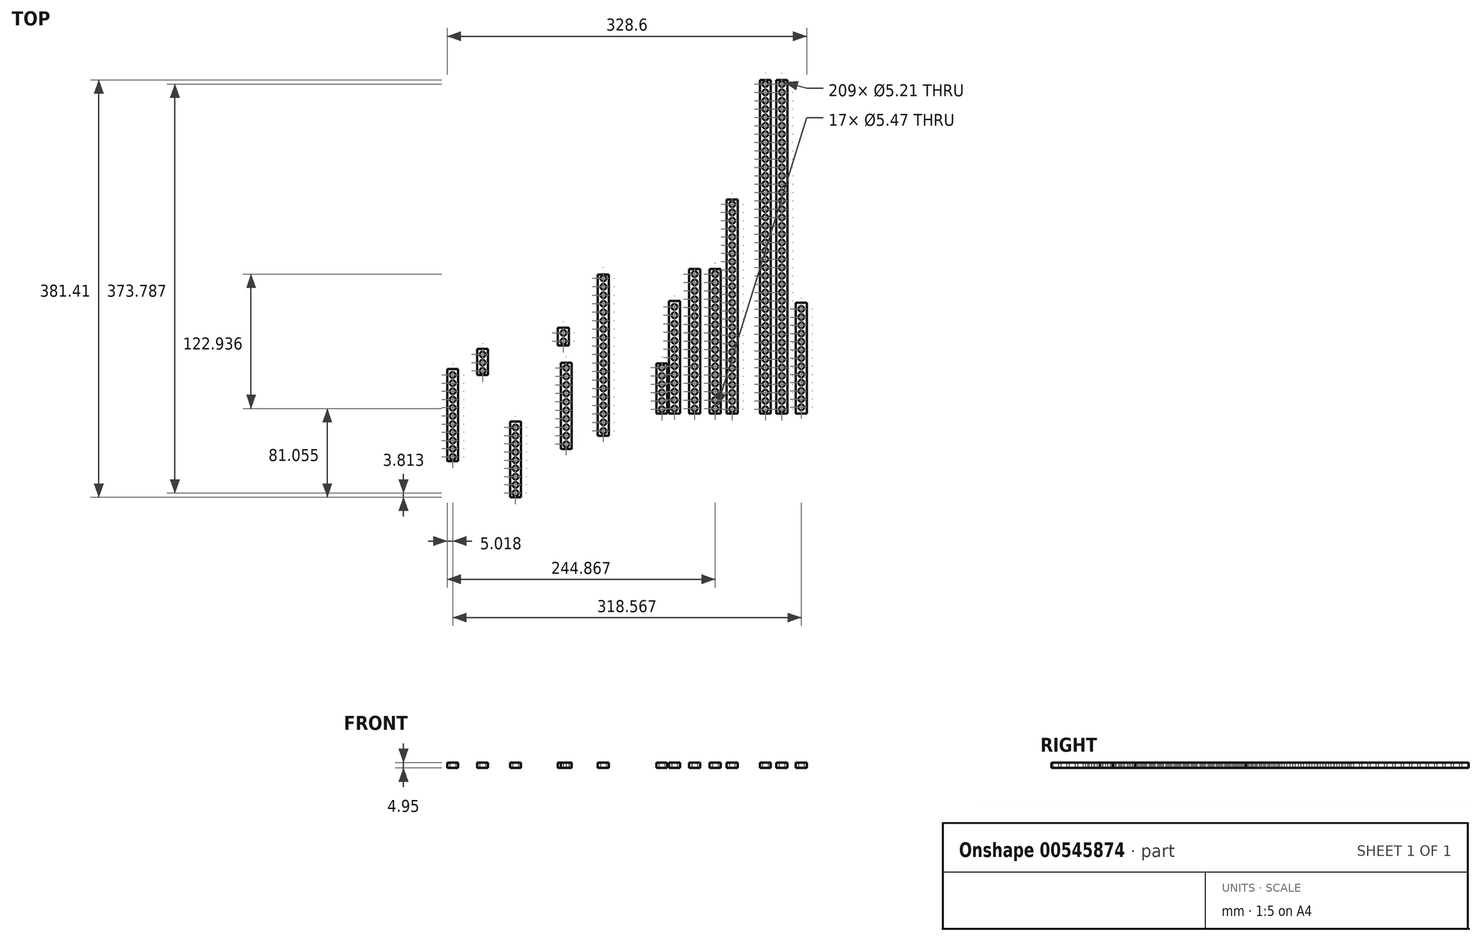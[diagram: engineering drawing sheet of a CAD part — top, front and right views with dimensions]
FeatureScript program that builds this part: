
annotation { "Feature Type Name" : "Feature", "Feature Type Description" : "" }
export const myFeature = defineFeature(function(context is Context, id is Id, definition is map)
    precondition{}
    {
        {
            var Q0;
            Q0=qCreatedBy(makeId("Top.planeOp"),FACE);
            var sketch = newSketch(context, id + "F0", { "sketchPlane" : qUnion([Q0])});
            skLineSegment(sketch, "E0.bottom", {"start": v(-63.67, 0) * mm, "end": v(-53.64, 0) * mm});
            skLineSegment(sketch, "E0.top", {"start": v(-63.67, 102.87) * mm, "end": v(-53.64, 102.87) * mm});
            skLineSegment(sketch, "E0.left", {"start": v(-63.67, 0) * mm, "end": v(-63.67, 102.87) * mm});
            skLineSegment(sketch, "E0.right", {"start": v(-53.64, 0) * mm, "end": v(-53.64, 102.87) * mm});
            skCircle(sketch, "E1", {"center": v(-58.66, 4.45) * mm, "radius": 2.6 * mm});
            skPoint(sketch, "E1.centerSnap0", {"position": v(-58.66, 0) * mm});
            skCircle(sketch, "E2.0.1.0", {"center": v(-58.66, 12.2) * mm, "radius": 2.6 * mm});
            skCircle(sketch, "E2.0.2.0", {"center": v(-58.66, 19.94) * mm, "radius": 2.6 * mm});
            skCircle(sketch, "E2.0.3.0", {"center": v(-58.66, 27.69) * mm, "radius": 2.6 * mm});
            skCircle(sketch, "E2.0.4.0", {"center": v(-58.66, 35.43) * mm, "radius": 2.6 * mm});
            skCircle(sketch, "E2.0.5.0", {"center": v(-58.66, 43.18) * mm, "radius": 2.6 * mm});
            skCircle(sketch, "E2.0.6.0", {"center": v(-58.66, 50.93) * mm, "radius": 2.6 * mm});
            skCircle(sketch, "E2.0.7.0", {"center": v(-58.66, 58.67) * mm, "radius": 2.6 * mm});
            skCircle(sketch, "E2.0.8.0", {"center": v(-58.66, 66.42) * mm, "radius": 2.6 * mm});
            skCircle(sketch, "E2.0.9.0", {"center": v(-58.66, 74.17) * mm, "radius": 2.6 * mm});
            skCircle(sketch, "E2.0.10.0", {"center": v(-58.66, 81.92) * mm, "radius": 2.6 * mm});
            skCircle(sketch, "E2.0.11.0", {"center": v(-58.66, 89.66) * mm, "radius": 2.6 * mm});
            skCircle(sketch, "E2.0.12.0", {"center": v(-58.66, 97.4) * mm, "radius": 2.6 * mm});
            skLineSegment(sketch, "E2.direction1", {"start": v(-58.66, 4.45) * mm, "end": v(-33.26, 4.45) * mm, "construction": true});
            skLineSegment(sketch, "E2.direction2", {"start": v(-58.66, 4.45) * mm, "end": v(-58.66, 12.2) * mm, "construction": true});
            skSolve(sketch);
        }
        {
            var Q0;
            Q0=makeQuery(id+"F0.imprint","IMPRINT",FACE,{"disambiguationData":[TD([[makeQuery(id+"F0.imprint","IMPRINT",EDGE,{"derivedFrom":sQuery(id+"F0.wireOp",EDGE,"E0.bottom")}),1.0]])]});
            extrude(context, id + "F1", {"entities" : qUnion([Q0]), "depth" : 4.95 * mm, "offsetDistance" : 25.4 * mm});
        }
        {
            var Q0;
            Q0=qCreatedBy(makeId("Top.planeOp"),FACE);
            var sketch = newSketch(context, id + "F2", { "sketchPlane" : qUnion([Q0])});
            skLineSegment(sketch, "E3.bottom", {"start": v(-45.23, 0) * mm, "end": v(-35.2, 0) * mm});
            skLineSegment(sketch, "E3.top", {"start": v(-45.23, 132.08) * mm, "end": v(-35.2, 132.08) * mm});
            skLineSegment(sketch, "E3.left", {"start": v(-45.23, 0) * mm, "end": v(-45.23, 132.08) * mm});
            skLineSegment(sketch, "E3.right", {"start": v(-35.2, 0) * mm, "end": v(-35.2, 132.08) * mm});
            skCircle(sketch, "E4", {"center": v(-40.2, 4.44) * mm, "radius": 2.6 * mm});
            skPoint(sketch, "E4.centerSnap0", {"position": v(-40.2, 0) * mm});
            skCircle(sketch, "E5.0.1.0", {"center": v(-40.2, 12.13) * mm, "radius": 2.6 * mm});
            skCircle(sketch, "E5.0.2.0", {"center": v(-40.2, 19.81) * mm, "radius": 2.6 * mm});
            skCircle(sketch, "E5.0.3.0", {"center": v(-40.2, 27.5) * mm, "radius": 2.6 * mm});
            skCircle(sketch, "E5.0.4.0", {"center": v(-40.2, 35.18) * mm, "radius": 2.6 * mm});
            skCircle(sketch, "E5.0.5.0", {"center": v(-40.2, 42.86) * mm, "radius": 2.6 * mm});
            skCircle(sketch, "E5.0.6.0", {"center": v(-40.2, 50.55) * mm, "radius": 2.6 * mm});
            skCircle(sketch, "E5.0.7.0", {"center": v(-40.2, 58.23) * mm, "radius": 2.6 * mm});
            skCircle(sketch, "E5.0.8.0", {"center": v(-40.2, 65.91) * mm, "radius": 2.6 * mm});
            skCircle(sketch, "E5.0.9.0", {"center": v(-40.2, 73.6) * mm, "radius": 2.6 * mm});
            skCircle(sketch, "E5.0.10.0", {"center": v(-40.2, 81.28) * mm, "radius": 2.6 * mm});
            skCircle(sketch, "E5.0.11.0", {"center": v(-40.2, 88.96) * mm, "radius": 2.6 * mm});
            skCircle(sketch, "E5.0.12.0", {"center": v(-40.2, 96.65) * mm, "radius": 2.6 * mm});
            skCircle(sketch, "E5.0.13.0", {"center": v(-40.2, 104.33) * mm, "radius": 2.6 * mm});
            skCircle(sketch, "E5.0.14.0", {"center": v(-40.2, 112.01) * mm, "radius": 2.6 * mm});
            skCircle(sketch, "E5.0.15.0", {"center": v(-40.2, 119.7) * mm, "radius": 2.6 * mm});
            skCircle(sketch, "E5.0.16.0", {"center": v(-40.2, 127.38) * mm, "radius": 2.6 * mm});
            skLineSegment(sketch, "E5.direction1", {"start": v(-40.2, 4.44) * mm, "end": v(-14.8, 4.45) * mm, "construction": true});
            skLineSegment(sketch, "E5.direction2", {"start": v(-40.2, 4.44) * mm, "end": v(-40.2, 12.13) * mm, "construction": true});
            skSolve(sketch);
        }
        {
            var Q0;
            Q0=makeQuery(id+"F2.imprint","IMPRINT",FACE,{"disambiguationData":[TD([[makeQuery(id+"F2.imprint","IMPRINT",EDGE,{"derivedFrom":sQuery(id+"F2.wireOp",EDGE,"E3.bottom")}),1.0]])]});
            extrude(context, id + "F3", {"entities" : qUnion([Q0]), "depth" : 4.95 * mm, "offsetDistance" : 25.4 * mm});
        }
        {
            var Q0;
            Q0=qCreatedBy(makeId("Top.planeOp"),FACE);
            var sketch = newSketch(context, id + "F4", { "sketchPlane" : qUnion([Q0])});
            skLineSegment(sketch, "E6.bottom", {"start": v(-26.44, 0) * mm, "end": v(-16.4, 0) * mm});
            skLineSegment(sketch, "E6.top", {"start": v(-26.44, 132.08) * mm, "end": v(-16.4, 132.08) * mm});
            skLineSegment(sketch, "E6.left", {"start": v(-26.44, 0) * mm, "end": v(-26.44, 132.08) * mm});
            skLineSegment(sketch, "E6.right", {"start": v(-16.4, 0) * mm, "end": v(-16.4, 132.08) * mm});
            skCircle(sketch, "E7", {"center": v(-21.42, 4.45) * mm, "radius": 2.73 * mm});
            skPoint(sketch, "E7.centerSnap0", {"position": v(-21.42, 0) * mm});
            skCircle(sketch, "E8.0.1.0", {"center": v(-21.42, 12.13) * mm, "radius": 2.73 * mm});
            skCircle(sketch, "E8.0.2.0", {"center": v(-21.42, 19.81) * mm, "radius": 2.73 * mm});
            skCircle(sketch, "E8.0.3.0", {"center": v(-21.42, 27.5) * mm, "radius": 2.73 * mm});
            skCircle(sketch, "E8.0.4.0", {"center": v(-21.42, 35.18) * mm, "radius": 2.73 * mm});
            skCircle(sketch, "E8.0.5.0", {"center": v(-21.42, 42.86) * mm, "radius": 2.73 * mm});
            skCircle(sketch, "E8.0.6.0", {"center": v(-21.42, 50.55) * mm, "radius": 2.73 * mm});
            skCircle(sketch, "E8.0.7.0", {"center": v(-21.42, 58.23) * mm, "radius": 2.73 * mm});
            skCircle(sketch, "E8.0.8.0", {"center": v(-21.42, 65.91) * mm, "radius": 2.73 * mm});
            skCircle(sketch, "E8.0.9.0", {"center": v(-21.42, 73.6) * mm, "radius": 2.73 * mm});
            skCircle(sketch, "E8.0.10.0", {"center": v(-21.42, 81.28) * mm, "radius": 2.73 * mm});
            skCircle(sketch, "E8.0.11.0", {"center": v(-21.42, 88.96) * mm, "radius": 2.73 * mm});
            skCircle(sketch, "E8.0.12.0", {"center": v(-21.42, 96.65) * mm, "radius": 2.73 * mm});
            skCircle(sketch, "E8.0.13.0", {"center": v(-21.42, 104.33) * mm, "radius": 2.73 * mm});
            skCircle(sketch, "E8.0.14.0", {"center": v(-21.42, 112.01) * mm, "radius": 2.73 * mm});
            skCircle(sketch, "E8.0.15.0", {"center": v(-21.42, 119.7) * mm, "radius": 2.73 * mm});
            skCircle(sketch, "E8.0.16.0", {"center": v(-21.42, 127.38) * mm, "radius": 2.73 * mm});
            skLineSegment(sketch, "E8.direction1", {"start": v(-21.42, 4.45) * mm, "end": v(3.98, 4.45) * mm, "construction": true});
            skLineSegment(sketch, "E8.direction2", {"start": v(-21.42, 4.45) * mm, "end": v(-21.42, 12.13) * mm, "construction": true});
            skSolve(sketch);
        }
        {
            var Q0;
            Q0=makeQuery(id+"F4.imprint","IMPRINT",FACE,{"disambiguationData":[TD([[makeQuery(id+"F4.imprint","IMPRINT",EDGE,{"derivedFrom":sQuery(id+"F4.wireOp",EDGE,"E6.bottom")}),1.0]])]});
            extrude(context, id + "F5", {"entities" : qUnion([Q0]), "depth" : 4.95 * mm, "offsetDistance" : 25.4 * mm});
        }
        {
            var Q0;
            Q0=qCreatedBy(makeId("Top.planeOp"),FACE);
            var sketch = newSketch(context, id + "F6", { "sketchPlane" : qUnion([Q0])});
            skLineSegment(sketch, "E9.bottom", {"start": v(-10.83, 0) * mm, "end": v(-0.8, 0) * mm});
            skLineSegment(sketch, "E9.top", {"start": v(-10.83, 195.58) * mm, "end": v(-0.8, 195.58) * mm});
            skLineSegment(sketch, "E9.left", {"start": v(-10.83, 0) * mm, "end": v(-10.83, 195.58) * mm});
            skLineSegment(sketch, "E9.right", {"start": v(-0.8, 0) * mm, "end": v(-0.8, 195.58) * mm});
            skCircle(sketch, "E10", {"center": v(-5.81, 3.81) * mm, "radius": 2.6 * mm});
            skPoint(sketch, "E10.centerSnap0", {"position": v(-5.81, 0) * mm});
            skCircle(sketch, "E11.0.1.0", {"center": v(-5.81, 11.3) * mm, "radius": 2.6 * mm});
            skCircle(sketch, "E11.0.2.0", {"center": v(-5.81, 18.8) * mm, "radius": 2.6 * mm});
            skCircle(sketch, "E11.0.3.0", {"center": v(-5.81, 26.29) * mm, "radius": 2.6 * mm});
            skCircle(sketch, "E11.0.4.0", {"center": v(-5.81, 33.78) * mm, "radius": 2.6 * mm});
            skCircle(sketch, "E11.0.5.0", {"center": v(-5.81, 41.28) * mm, "radius": 2.6 * mm});
            skCircle(sketch, "E11.0.6.0", {"center": v(-5.81, 48.77) * mm, "radius": 2.6 * mm});
            skCircle(sketch, "E11.0.7.0", {"center": v(-5.81, 56.26) * mm, "radius": 2.6 * mm});
            skCircle(sketch, "E11.0.8.0", {"center": v(-5.81, 63.75) * mm, "radius": 2.6 * mm});
            skCircle(sketch, "E11.0.9.0", {"center": v(-5.81, 71.25) * mm, "radius": 2.6 * mm});
            skCircle(sketch, "E11.0.10.0", {"center": v(-5.81, 78.74) * mm, "radius": 2.6 * mm});
            skCircle(sketch, "E11.0.11.0", {"center": v(-5.81, 86.23) * mm, "radius": 2.6 * mm});
            skCircle(sketch, "E11.0.12.0", {"center": v(-5.81, 93.73) * mm, "radius": 2.6 * mm});
            skCircle(sketch, "E11.0.13.0", {"center": v(-5.81, 101.22) * mm, "radius": 2.6 * mm});
            skCircle(sketch, "E11.0.14.0", {"center": v(-5.81, 108.71) * mm, "radius": 2.6 * mm});
            skCircle(sketch, "E11.0.15.0", {"center": v(-5.81, 116.2) * mm, "radius": 2.6 * mm});
            skCircle(sketch, "E11.0.16.0", {"center": v(-5.81, 123.7) * mm, "radius": 2.6 * mm});
            skCircle(sketch, "E11.0.17.0", {"center": v(-5.81, 131.2) * mm, "radius": 2.6 * mm});
            skCircle(sketch, "E11.0.18.0", {"center": v(-5.81, 138.68) * mm, "radius": 2.6 * mm});
            skCircle(sketch, "E11.0.19.0", {"center": v(-5.81, 146.18) * mm, "radius": 2.6 * mm});
            skCircle(sketch, "E11.0.20.0", {"center": v(-5.81, 153.67) * mm, "radius": 2.6 * mm});
            skCircle(sketch, "E11.0.21.0", {"center": v(-5.81, 161.16) * mm, "radius": 2.6 * mm});
            skCircle(sketch, "E11.0.22.0", {"center": v(-5.81, 168.66) * mm, "radius": 2.6 * mm});
            skCircle(sketch, "E11.0.23.0", {"center": v(-5.81, 176.15) * mm, "radius": 2.6 * mm});
            skCircle(sketch, "E11.0.24.0", {"center": v(-5.81, 183.64) * mm, "radius": 2.6 * mm});
            skCircle(sketch, "E11.0.25.0", {"center": v(-5.81, 191.14) * mm, "radius": 2.6 * mm});
            skLineSegment(sketch, "E11.direction1", {"start": v(-5.81, 3.81) * mm, "end": v(19.59, 3.81) * mm, "construction": true});
            skLineSegment(sketch, "E11.direction2", {"start": v(-5.81, 3.81) * mm, "end": v(-5.81, 11.3) * mm, "construction": true});
            skSolve(sketch);
        }
        {
            var Q0;
            Q0=makeQuery(id+"F6.imprint","IMPRINT",FACE,{"disambiguationData":[TD([[makeQuery(id+"F6.imprint","IMPRINT",EDGE,{"derivedFrom":sQuery(id+"F6.wireOp",EDGE,"E9.bottom")}),1.0]])]});
            var Q1;
            Q1=makeQuery(id+"F6.imprint","IMPRINT",FACE,{"disambiguationData":[TD([[makeQuery(id+"F6.imprint","IMPRINT",EDGE,{"derivedFrom":sQuery(id+"F6.wireOp",EDGE,"ulNz63qi-A0Wq-LpTq-UIq0-C9iqN6fXD88K.bottom")}),1.0]])]});
            extrude(context, id + "F7", {"entities" : qUnion([Q0, Q1]), "depth" : 4.95 * mm, "offsetDistance" : 25.4 * mm});
        }
        {
            var Q0;
            Q0=qCreatedBy(makeId("Top.planeOp"),FACE);
            var sketch = newSketch(context, id + "F8", { "sketchPlane" : qUnion([Q0])});
            skLineSegment(sketch, "E12.bottom", {"start": v(19.42, 0) * mm, "end": v(29.46, 0) * mm});
            skLineSegment(sketch, "E12.top", {"start": v(19.42, 304.8) * mm, "end": v(29.46, 304.8) * mm});
            skLineSegment(sketch, "E12.left", {"start": v(19.42, 0) * mm, "end": v(19.42, 304.8) * mm});
            skLineSegment(sketch, "E12.right", {"start": v(29.46, 0) * mm, "end": v(29.46, 304.8) * mm});
            skCircle(sketch, "E13", {"center": v(24.44, 3.81) * mm, "radius": 2.6 * mm});
            skPoint(sketch, "E13.centerSnap0", {"position": v(24.44, 0) * mm});
            skLineSegment(sketch, "E14.bottom", {"start": v(34.54, 0) * mm, "end": v(44.57, 0) * mm});
            skLineSegment(sketch, "E14.top", {"start": v(34.54, 304.8) * mm, "end": v(44.57, 304.8) * mm});
            skLineSegment(sketch, "E14.left", {"start": v(34.54, 0) * mm, "end": v(34.54, 304.8) * mm});
            skLineSegment(sketch, "E14.right", {"start": v(44.57, 0) * mm, "end": v(44.57, 304.8) * mm});
            skCircle(sketch, "E15.0.1.0", {"center": v(24.44, 11.43) * mm, "radius": 2.6 * mm});
            skCircle(sketch, "E15.0.2.0", {"center": v(24.44, 19.05) * mm, "radius": 2.6 * mm});
            skCircle(sketch, "E15.0.3.0", {"center": v(24.44, 26.67) * mm, "radius": 2.6 * mm});
            skCircle(sketch, "E15.0.4.0", {"center": v(24.44, 34.3) * mm, "radius": 2.6 * mm});
            skCircle(sketch, "E15.0.5.0", {"center": v(24.44, 41.91) * mm, "radius": 2.6 * mm});
            skCircle(sketch, "E15.0.6.0", {"center": v(24.44, 49.53) * mm, "radius": 2.6 * mm});
            skCircle(sketch, "E15.0.7.0", {"center": v(24.44, 57.15) * mm, "radius": 2.6 * mm});
            skCircle(sketch, "E15.0.8.0", {"center": v(24.44, 64.77) * mm, "radius": 2.6 * mm});
            skCircle(sketch, "E15.0.9.0", {"center": v(24.44, 72.4) * mm, "radius": 2.6 * mm});
            skCircle(sketch, "E15.0.10.0", {"center": v(24.44, 80) * mm, "radius": 2.6 * mm});
            skCircle(sketch, "E15.0.11.0", {"center": v(24.44, 87.63) * mm, "radius": 2.6 * mm});
            skCircle(sketch, "E15.0.12.0", {"center": v(24.44, 95.25) * mm, "radius": 2.6 * mm});
            skCircle(sketch, "E15.0.13.0", {"center": v(24.44, 102.87) * mm, "radius": 2.6 * mm});
            skCircle(sketch, "E15.0.14.0", {"center": v(24.44, 110.5) * mm, "radius": 2.6 * mm});
            skCircle(sketch, "E15.0.15.0", {"center": v(24.44, 118.11) * mm, "radius": 2.6 * mm});
            skCircle(sketch, "E15.0.16.0", {"center": v(24.44, 125.73) * mm, "radius": 2.6 * mm});
            skCircle(sketch, "E15.0.17.0", {"center": v(24.44, 133.35) * mm, "radius": 2.6 * mm});
            skCircle(sketch, "E15.0.18.0", {"center": v(24.44, 140.97) * mm, "radius": 2.6 * mm});
            skCircle(sketch, "E15.0.19.0", {"center": v(24.44, 148.6) * mm, "radius": 2.6 * mm});
            skCircle(sketch, "E15.0.20.0", {"center": v(24.44, 156.21) * mm, "radius": 2.6 * mm});
            skCircle(sketch, "E15.0.21.0", {"center": v(24.44, 163.83) * mm, "radius": 2.6 * mm});
            skCircle(sketch, "E15.0.22.0", {"center": v(24.44, 171.45) * mm, "radius": 2.6 * mm});
            skCircle(sketch, "E15.0.23.0", {"center": v(24.44, 179.07) * mm, "radius": 2.6 * mm});
            skCircle(sketch, "E15.0.24.0", {"center": v(24.44, 186.7) * mm, "radius": 2.6 * mm});
            skCircle(sketch, "E15.0.25.0", {"center": v(24.44, 194.3) * mm, "radius": 2.6 * mm});
            skCircle(sketch, "E15.0.26.0", {"center": v(24.44, 201.93) * mm, "radius": 2.6 * mm});
            skCircle(sketch, "E15.0.27.0", {"center": v(24.44, 209.55) * mm, "radius": 2.6 * mm});
            skCircle(sketch, "E15.0.28.0", {"center": v(24.44, 217.17) * mm, "radius": 2.6 * mm});
            skCircle(sketch, "E15.0.29.0", {"center": v(24.44, 224.8) * mm, "radius": 2.6 * mm});
            skCircle(sketch, "E15.0.30.0", {"center": v(24.44, 232.4) * mm, "radius": 2.6 * mm});
            skCircle(sketch, "E15.0.31.0", {"center": v(24.44, 240.03) * mm, "radius": 2.6 * mm});
            skCircle(sketch, "E15.0.32.0", {"center": v(24.44, 247.65) * mm, "radius": 2.6 * mm});
            skCircle(sketch, "E15.0.33.0", {"center": v(24.44, 255.27) * mm, "radius": 2.6 * mm});
            skCircle(sketch, "E15.0.34.0", {"center": v(24.44, 262.89) * mm, "radius": 2.6 * mm});
            skCircle(sketch, "E15.0.35.0", {"center": v(24.44, 270.5) * mm, "radius": 2.6 * mm});
            skCircle(sketch, "E15.0.36.0", {"center": v(24.44, 278.13) * mm, "radius": 2.6 * mm});
            skCircle(sketch, "E15.0.37.0", {"center": v(24.44, 285.75) * mm, "radius": 2.6 * mm});
            skCircle(sketch, "E15.0.38.0", {"center": v(24.44, 293.37) * mm, "radius": 2.6 * mm});
            skCircle(sketch, "E15.0.39.0", {"center": v(24.44, 300.99) * mm, "radius": 2.6 * mm});
            skCircle(sketch, "E15.1.0.0", {"center": v(39.55, 3.81) * mm, "radius": 2.6 * mm});
            skCircle(sketch, "E15.1.1.0", {"center": v(39.55, 11.43) * mm, "radius": 2.6 * mm});
            skCircle(sketch, "E15.1.2.0", {"center": v(39.55, 19.05) * mm, "radius": 2.6 * mm});
            skCircle(sketch, "E15.1.3.0", {"center": v(39.55, 26.67) * mm, "radius": 2.6 * mm});
            skCircle(sketch, "E15.1.4.0", {"center": v(39.55, 34.3) * mm, "radius": 2.6 * mm});
            skCircle(sketch, "E15.1.5.0", {"center": v(39.55, 41.91) * mm, "radius": 2.6 * mm});
            skCircle(sketch, "E15.1.6.0", {"center": v(39.55, 49.53) * mm, "radius": 2.6 * mm});
            skCircle(sketch, "E15.1.7.0", {"center": v(39.55, 57.15) * mm, "radius": 2.6 * mm});
            skCircle(sketch, "E15.1.8.0", {"center": v(39.55, 64.77) * mm, "radius": 2.6 * mm});
            skCircle(sketch, "E15.1.9.0", {"center": v(39.55, 72.4) * mm, "radius": 2.6 * mm});
            skCircle(sketch, "E15.1.10.0", {"center": v(39.55, 80) * mm, "radius": 2.6 * mm});
            skCircle(sketch, "E15.1.11.0", {"center": v(39.55, 87.63) * mm, "radius": 2.6 * mm});
            skCircle(sketch, "E15.1.12.0", {"center": v(39.55, 95.25) * mm, "radius": 2.6 * mm});
            skCircle(sketch, "E15.1.13.0", {"center": v(39.55, 102.87) * mm, "radius": 2.6 * mm});
            skCircle(sketch, "E15.1.14.0", {"center": v(39.55, 110.5) * mm, "radius": 2.6 * mm});
            skCircle(sketch, "E15.1.15.0", {"center": v(39.55, 118.11) * mm, "radius": 2.6 * mm});
            skCircle(sketch, "E15.1.16.0", {"center": v(39.55, 125.73) * mm, "radius": 2.6 * mm});
            skCircle(sketch, "E15.1.17.0", {"center": v(39.55, 133.35) * mm, "radius": 2.6 * mm});
            skCircle(sketch, "E15.1.18.0", {"center": v(39.55, 140.97) * mm, "radius": 2.6 * mm});
            skCircle(sketch, "E15.1.19.0", {"center": v(39.55, 148.6) * mm, "radius": 2.6 * mm});
            skCircle(sketch, "E15.1.20.0", {"center": v(39.55, 156.21) * mm, "radius": 2.6 * mm});
            skCircle(sketch, "E15.1.21.0", {"center": v(39.55, 163.83) * mm, "radius": 2.6 * mm});
            skCircle(sketch, "E15.1.22.0", {"center": v(39.55, 171.45) * mm, "radius": 2.6 * mm});
            skCircle(sketch, "E15.1.23.0", {"center": v(39.55, 179.07) * mm, "radius": 2.6 * mm});
            skCircle(sketch, "E15.1.24.0", {"center": v(39.55, 186.7) * mm, "radius": 2.6 * mm});
            skCircle(sketch, "E15.1.25.0", {"center": v(39.55, 194.3) * mm, "radius": 2.6 * mm});
            skCircle(sketch, "E15.1.26.0", {"center": v(39.55, 201.93) * mm, "radius": 2.6 * mm});
            skCircle(sketch, "E15.1.27.0", {"center": v(39.55, 209.55) * mm, "radius": 2.6 * mm});
            skCircle(sketch, "E15.1.28.0", {"center": v(39.55, 217.17) * mm, "radius": 2.6 * mm});
            skCircle(sketch, "E15.1.29.0", {"center": v(39.55, 224.8) * mm, "radius": 2.6 * mm});
            skCircle(sketch, "E15.1.30.0", {"center": v(39.55, 232.4) * mm, "radius": 2.6 * mm});
            skCircle(sketch, "E15.1.31.0", {"center": v(39.55, 240.03) * mm, "radius": 2.6 * mm});
            skCircle(sketch, "E15.1.32.0", {"center": v(39.55, 247.65) * mm, "radius": 2.6 * mm});
            skCircle(sketch, "E15.1.33.0", {"center": v(39.55, 255.27) * mm, "radius": 2.6 * mm});
            skCircle(sketch, "E15.1.34.0", {"center": v(39.55, 262.89) * mm, "radius": 2.6 * mm});
            skCircle(sketch, "E15.1.35.0", {"center": v(39.55, 270.5) * mm, "radius": 2.6 * mm});
            skCircle(sketch, "E15.1.36.0", {"center": v(39.55, 278.13) * mm, "radius": 2.6 * mm});
            skCircle(sketch, "E15.1.37.0", {"center": v(39.55, 285.75) * mm, "radius": 2.6 * mm});
            skCircle(sketch, "E15.1.38.0", {"center": v(39.55, 293.37) * mm, "radius": 2.6 * mm});
            skCircle(sketch, "E15.1.39.0", {"center": v(39.55, 300.99) * mm, "radius": 2.6 * mm});
            skLineSegment(sketch, "E15.direction1", {"start": v(24.44, 4.45) * mm, "end": v(39.55, 4.45) * mm, "construction": true});
            skLineSegment(sketch, "E15.direction2", {"start": v(24.44, 4.45) * mm, "end": v(24.44, 12.07) * mm, "construction": true});
            skSolve(sketch);
        }
        {
            var Q0;
            Q0=makeQuery(id+"F8.imprint","IMPRINT",FACE,{"disambiguationData":[TD([[makeQuery(id+"F8.imprint","IMPRINT",EDGE,{"derivedFrom":sQuery(id+"F8.wireOp",EDGE,"E12.bottom")}),1.0]])]});
            var Q1;
            Q1=makeQuery(id+"F8.imprint","IMPRINT",FACE,{"disambiguationData":[TD([[makeQuery(id+"F8.imprint","IMPRINT",EDGE,{"derivedFrom":sQuery(id+"F8.wireOp",EDGE,"E14.bottom")}),1.0]])]});
            extrude(context, id + "F9", {"entities" : qUnion([Q0, Q1]), "depth" : 4.95 * mm, "offsetDistance" : 25.4 * mm});
        }
        {
            var Q0;
            Q0=qCreatedBy(makeId("Top.planeOp"),FACE);
            var sketch = newSketch(context, id + "F10", { "sketchPlane" : qUnion([Q0])});
            skLineSegment(sketch, "E16.bottom", {"start": v(52.28, 0) * mm, "end": v(62.31, 0) * mm});
            skLineSegment(sketch, "E16.top", {"start": v(52.28, 101.22) * mm, "end": v(62.31, 101.22) * mm});
            skLineSegment(sketch, "E16.left", {"start": v(52.28, 0) * mm, "end": v(52.28, 101.22) * mm});
            skLineSegment(sketch, "E16.right", {"start": v(62.31, 0) * mm, "end": v(62.31, 101.22) * mm});
            skCircle(sketch, "E17", {"center": v(57.3, 5.59) * mm, "radius": 2.6 * mm});
            skPoint(sketch, "E17.centerSnap0", {"position": v(57.3, 0) * mm});
            skCircle(sketch, "E18.0.1.0", {"center": v(57.3, 13.08) * mm, "radius": 2.6 * mm});
            skCircle(sketch, "E18.0.2.0", {"center": v(57.3, 20.57) * mm, "radius": 2.6 * mm});
            skCircle(sketch, "E18.0.3.0", {"center": v(57.3, 28.07) * mm, "radius": 2.6 * mm});
            skCircle(sketch, "E18.0.4.0", {"center": v(57.3, 35.56) * mm, "radius": 2.6 * mm});
            skCircle(sketch, "E18.0.5.0", {"center": v(57.3, 43.05) * mm, "radius": 2.6 * mm});
            skCircle(sketch, "E18.0.6.0", {"center": v(57.3, 50.55) * mm, "radius": 2.6 * mm});
            skCircle(sketch, "E18.0.7.0", {"center": v(57.3, 58.04) * mm, "radius": 2.6 * mm});
            skCircle(sketch, "E18.0.8.0", {"center": v(57.3, 65.53) * mm, "radius": 2.6 * mm});
            skCircle(sketch, "E18.0.9.0", {"center": v(57.3, 73.03) * mm, "radius": 2.6 * mm});
            skCircle(sketch, "E18.0.10.0", {"center": v(57.3, 80.52) * mm, "radius": 2.6 * mm});
            skCircle(sketch, "E18.0.11.0", {"center": v(57.3, 88.01) * mm, "radius": 2.6 * mm});
            skCircle(sketch, "E18.0.12.0", {"center": v(57.3, 95.5) * mm, "radius": 2.6 * mm});
            skLineSegment(sketch, "E18.direction1", {"start": v(57.3, 5.59) * mm, "end": v(82.7, 5.59) * mm, "construction": true});
            skLineSegment(sketch, "E18.direction2", {"start": v(57.3, 5.59) * mm, "end": v(57.3, 13.08) * mm, "construction": true});
            skSolve(sketch);
        }
        {
            var Q0;
            Q0=makeQuery(id+"F10.imprint","IMPRINT",FACE,{"disambiguationData":[TD([[makeQuery(id+"F10.imprint","IMPRINT",EDGE,{"derivedFrom":sQuery(id+"F10.wireOp",EDGE,"E16.bottom")}),1.0]])]});
            var Q1;
            Q1=makeQuery(id+"F10.imprint","IMPRINT",FACE,{"disambiguationData":[TD([[makeQuery(id+"F10.imprint","IMPRINT",EDGE,{"derivedFrom":sQuery(id+"F10.wireOp",EDGE,"RP2cDaQo-Igoh-qRva-gbff-8Lfj2EcFQpCx.bottom")}),1.0]])]});
            extrude(context, id + "F11", {"entities" : qUnion([Q0, Q1]), "depth" : 4.95 * mm, "offsetDistance" : 25.4 * mm});
        }
        {
            var Q0;
            Q0=qCreatedBy(makeId("Top.planeOp"),FACE);
            var sketch = newSketch(context, id + "F12", { "sketchPlane" : qUnion([Q0])});
            skLineSegment(sketch, "E19.bottom", {"start": v(-75.17, 0) * mm, "end": v(-65.14, 0) * mm});
            skLineSegment(sketch, "E19.top", {"start": v(-75.17, 45.72) * mm, "end": v(-65.14, 45.72) * mm});
            skLineSegment(sketch, "E19.left", {"start": v(-75.17, 0) * mm, "end": v(-75.17, 45.72) * mm});
            skLineSegment(sketch, "E19.right", {"start": v(-65.14, 0) * mm, "end": v(-65.14, 45.72) * mm});
            skLineSegment(sketch, "E20", {"start": v(-70.16, 0) * mm, "end": v(-70.16, 3.81) * mm, "construction": true});
            skCircle(sketch, "E21", {"center": v(-70.16, 3.81) * mm, "radius": 2.6 * mm});
            skCircle(sketch, "E22.0.1.0", {"center": v(-70.16, 11.43) * mm, "radius": 2.6 * mm});
            skCircle(sketch, "E22.0.2.0", {"center": v(-70.16, 19.05) * mm, "radius": 2.6 * mm});
            skCircle(sketch, "E22.0.3.0", {"center": v(-70.16, 26.67) * mm, "radius": 2.6 * mm});
            skCircle(sketch, "E22.0.4.0", {"center": v(-70.16, 34.29) * mm, "radius": 2.6 * mm});
            skCircle(sketch, "E22.0.5.0", {"center": v(-70.16, 41.9) * mm, "radius": 2.6 * mm});
            skLineSegment(sketch, "E22.direction1", {"start": v(-70.16, 4.45) * mm, "end": v(-44.76, 4.45) * mm, "construction": true});
            skLineSegment(sketch, "E22.direction2", {"start": v(-70.16, 4.45) * mm, "end": v(-70.16, 12.06) * mm, "construction": true});
            skSolve(sketch);
        }
        {
            var Q0;
            Q0=makeQuery(id+"F12.imprint","IMPRINT",FACE,{"disambiguationData":[TD([[makeQuery(id+"F12.imprint","IMPRINT",EDGE,{"derivedFrom":sQuery(id+"F12.wireOp",EDGE,"E19.bottom")}),1.0]])]});
            extrude(context, id + "F13", {"entities" : qUnion([Q0]), "depth" : 4.95 * mm, "offsetDistance" : 25.4 * mm});
        }
        {
            var Q0;
            Q0=qCreatedBy(makeId("Top.planeOp"),FACE);
            var sketch = newSketch(context, id + "F14", { "sketchPlane" : qUnion([Q0])});
            skLineSegment(sketch, "E23.bottom", {"start": v(-128.6, -20.4) * mm, "end": v(-118.58, -20.4) * mm});
            skLineSegment(sketch, "E23.top", {"start": v(-128.6, 126.92) * mm, "end": v(-118.58, 126.92) * mm});
            skLineSegment(sketch, "E23.left", {"start": v(-128.6, -20.4) * mm, "end": v(-128.6, 126.92) * mm});
            skLineSegment(sketch, "E23.right", {"start": v(-118.58, -20.4) * mm, "end": v(-118.58, 126.92) * mm});
            skCircle(sketch, "E24", {"center": v(-123.6, -15.96) * mm, "radius": 2.6 * mm});
            skPoint(sketch, "E24.centerSnap0", {"position": v(-123.6, -20.4) * mm});
            skCircle(sketch, "E25.0.1.0", {"center": v(-123.6, -8.2) * mm, "radius": 2.6 * mm});
            skCircle(sketch, "E25.0.2.0", {"center": v(-123.6, -0.46) * mm, "radius": 2.6 * mm});
            skCircle(sketch, "E25.0.3.0", {"center": v(-123.6, 7.29) * mm, "radius": 2.6 * mm});
            skCircle(sketch, "E25.0.4.0", {"center": v(-123.6, 15.03) * mm, "radius": 2.6 * mm});
            skCircle(sketch, "E25.0.5.0", {"center": v(-123.6, 22.78) * mm, "radius": 2.6 * mm});
            skCircle(sketch, "E25.0.6.0", {"center": v(-123.6, 30.53) * mm, "radius": 2.6 * mm});
            skCircle(sketch, "E25.0.7.0", {"center": v(-123.6, 38.27) * mm, "radius": 2.6 * mm});
            skCircle(sketch, "E25.0.8.0", {"center": v(-123.6, 46.02) * mm, "radius": 2.6 * mm});
            skCircle(sketch, "E25.0.9.0", {"center": v(-123.6, 53.77) * mm, "radius": 2.6 * mm});
            skCircle(sketch, "E25.0.10.0", {"center": v(-123.6, 61.51) * mm, "radius": 2.6 * mm});
            skCircle(sketch, "E25.0.11.0", {"center": v(-123.6, 69.26) * mm, "radius": 2.6 * mm});
            skCircle(sketch, "E25.0.12.0", {"center": v(-123.6, 77) * mm, "radius": 2.6 * mm});
            skLineSegment(sketch, "E25.direction1", {"start": v(-123.6, -15.96) * mm, "end": v(-98.2, -15.96) * mm, "construction": true});
            skLineSegment(sketch, "E25.direction2", {"start": v(-123.6, -15.96) * mm, "end": v(-123.6, -8.2) * mm, "construction": true});
            skCircle(sketch, "E26.0.0.13", {"center": v(-123.6, 84.76) * mm, "radius": 2.6 * mm});
            skCircle(sketch, "E26.0.0.14", {"center": v(-123.6, 92.5) * mm, "radius": 2.6 * mm});
            skCircle(sketch, "E26.0.0.15", {"center": v(-123.6, 100.25) * mm, "radius": 2.6 * mm});
            skCircle(sketch, "E26.0.0.16", {"center": v(-123.6, 108) * mm, "radius": 2.6 * mm});
            skCircle(sketch, "E26.0.0.17", {"center": v(-123.6, 115.74) * mm, "radius": 2.6 * mm});
            skCircle(sketch, "E26.0.0.18", {"center": v(-123.6, 123.5) * mm, "radius": 2.6 * mm});
            skSolve(sketch);
        }
        {
            var Q0;
            Q0 = qSketchRegion(id + "F14", true);
            var Q1;
            Q1=makeQuery(id+"F13.opExtrude","CAP_FACE",FACE,{"disambiguationData":[OSD([sQuery(id+"F12.wireOp",EDGE,"E19.bottom"),sQuery(id+"F12.wireOp",EDGE,"E19.top"),sQuery(id+"F12.wireOp",EDGE,"E19.left"),sQuery(id+"F12.wireOp",EDGE,"E19.right"),sQuery(id+"F12.wireOp",EDGE,"E21"),sQuery(id+"F12.wireOp",EDGE,"E22.0.1.0"),sQuery(id+"F12.wireOp",EDGE,"E22.0.2.0"),sQuery(id+"F12.wireOp",EDGE,"E22.0.3.0"),sQuery(id+"F12.wireOp",EDGE,"E22.0.4.0"),sQuery(id+"F12.wireOp",EDGE,"E22.0.5.0")])],"isStart":false});
            extrude(context, id + "F15", {"entities" : qUnion([Q0]), "endBound" : BoundingType.UP_TO_SURFACE, "depth" : 25.4 * mm, "endBoundEntityFace" : qUnion([Q1]), "offsetDistance" : 25.4 * mm});
        }
        {
            var Q0;
            Q0=qCreatedBy(makeId("Top.planeOp"),FACE);
            var sketch = newSketch(context, id + "F16", { "sketchPlane" : qUnion([Q0])});
            skLineSegment(sketch, "E27.bottom", {"start": v(-162.53, -32.6) * mm, "end": v(-152.5, -32.6) * mm});
            skLineSegment(sketch, "E27.top", {"start": v(-162.53, 46.15) * mm, "end": v(-152.5, 46.15) * mm});
            skLineSegment(sketch, "E27.left", {"start": v(-162.53, -32.6) * mm, "end": v(-162.53, 46.15) * mm});
            skLineSegment(sketch, "E27.right", {"start": v(-152.5, -32.6) * mm, "end": v(-152.5, 46.15) * mm});
            skCircle(sketch, "E28", {"center": v(-157.5, -28.15) * mm, "radius": 2.6 * mm});
            skPoint(sketch, "E28.centerSnap0", {"position": v(-157.5, -32.6) * mm});
            skCircle(sketch, "E29.0.1.0", {"center": v(-157.5, -20.4) * mm, "radius": 2.6 * mm});
            skCircle(sketch, "E29.0.2.0", {"center": v(-157.5, -12.66) * mm, "radius": 2.6 * mm});
            skCircle(sketch, "E29.0.3.0", {"center": v(-157.5, -4.9) * mm, "radius": 2.6 * mm});
            skCircle(sketch, "E29.0.4.0", {"center": v(-157.5, 2.84) * mm, "radius": 2.6 * mm});
            skCircle(sketch, "E29.0.5.0", {"center": v(-157.5, 10.59) * mm, "radius": 2.6 * mm});
            skCircle(sketch, "E29.0.6.0", {"center": v(-157.5, 18.33) * mm, "radius": 2.6 * mm});
            skCircle(sketch, "E29.0.7.0", {"center": v(-157.5, 26.08) * mm, "radius": 2.6 * mm});
            skCircle(sketch, "E29.0.8.0", {"center": v(-157.5, 33.83) * mm, "radius": 2.6 * mm});
            skCircle(sketch, "E29.0.9.0", {"center": v(-157.5, 41.57) * mm, "radius": 2.6 * mm});
            skLineSegment(sketch, "E29.direction1", {"start": v(-157.5, -28.15) * mm, "end": v(-132.1, -28.15) * mm, "construction": true});
            skLineSegment(sketch, "E29.direction2", {"start": v(-157.5, -28.15) * mm, "end": v(-157.5, -20.4) * mm, "construction": true});
            skSolve(sketch);
        }
        {
            var Q0;
            Q0=makeQuery(id+"F16.imprint","IMPRINT",FACE,{"disambiguationData":[TD([[makeQuery(id+"F16.imprint","IMPRINT",EDGE,{"derivedFrom":sQuery(id+"F16.wireOp",EDGE,"E27.bottom")}),1.0]])]});
            var Q1;
            Q1=makeQuery(id+"F15.opExtrude","CAP_FACE",FACE,{"disambiguationData":[OSD([sQuery(id+"F14.wireOp",EDGE,"E23.bottom"),sQuery(id+"F14.wireOp",EDGE,"E23.top"),sQuery(id+"F14.wireOp",EDGE,"E23.left"),sQuery(id+"F14.wireOp",EDGE,"E23.right"),sQuery(id+"F14.wireOp",EDGE,"E24"),sQuery(id+"F14.wireOp",EDGE,"E25.0.1.0"),sQuery(id+"F14.wireOp",EDGE,"E25.0.2.0"),sQuery(id+"F14.wireOp",EDGE,"E25.0.3.0"),sQuery(id+"F14.wireOp",EDGE,"E25.0.4.0"),sQuery(id+"F14.wireOp",EDGE,"E25.0.5.0"),sQuery(id+"F14.wireOp",EDGE,"E25.0.6.0"),sQuery(id+"F14.wireOp",EDGE,"E25.0.7.0"),sQuery(id+"F14.wireOp",EDGE,"E25.0.8.0"),sQuery(id+"F14.wireOp",EDGE,"E25.0.9.0"),sQuery(id+"F14.wireOp",EDGE,"E25.0.10.0"),sQuery(id+"F14.wireOp",EDGE,"E25.0.11.0"),sQuery(id+"F14.wireOp",EDGE,"E25.0.12.0"),sQuery(id+"F14.wireOp",EDGE,"E26.0.0.13"),sQuery(id+"F14.wireOp",EDGE,"E26.0.0.14"),sQuery(id+"F14.wireOp",EDGE,"E26.0.0.15"),sQuery(id+"F14.wireOp",EDGE,"E26.0.0.16"),sQuery(id+"F14.wireOp",EDGE,"E26.0.0.17"),sQuery(id+"F14.wireOp",EDGE,"E26.0.0.18")])],"isStart":false});
            extrude(context, id + "F17", {"entities" : qUnion([Q0]), "endBound" : BoundingType.UP_TO_SURFACE, "depth" : 25.4 * mm, "endBoundEntityFace" : qUnion([Q1]), "offsetDistance" : 25.4 * mm});
        }
        {
            var Q0;
            Q0=qCreatedBy(makeId("Top.planeOp"),FACE);
            var sketch = newSketch(context, id + "F18", { "sketchPlane" : qUnion([Q0])});
            skLineSegment(sketch, "E30.bottom", {"start": v(-165.12, 62.1) * mm, "end": v(-155.08, 62.1) * mm});
            skLineSegment(sketch, "E30.top", {"start": v(-165.12, 78.23) * mm, "end": v(-155.08, 78.23) * mm});
            skLineSegment(sketch, "E30.left", {"start": v(-165.12, 62.1) * mm, "end": v(-165.12, 78.23) * mm});
            skLineSegment(sketch, "E30.right", {"start": v(-155.08, 62.1) * mm, "end": v(-155.08, 78.23) * mm});
            skLineSegment(sketch, "E31", {"start": v(-160.1, 62.1) * mm, "end": v(-160.1, 65.9) * mm, "construction": true});
            skCircle(sketch, "E32", {"center": v(-160.1, 65.9) * mm, "radius": 2.6 * mm});
            skCircle(sketch, "E33.0.1.0", {"center": v(-160.1, 73.52) * mm, "radius": 2.6 * mm});
            skLineSegment(sketch, "E33.direction2", {"start": v(-160.1, 66.54) * mm, "end": v(-160.1, 74.16) * mm, "construction": true});
            skSolve(sketch);
        }
        {
            var Q0;
            Q0 = qSketchRegion(id + "F18", true);
            var Q1;
            Q1=makeQuery(id+"F17.opExtrude","CAP_FACE",FACE,{"disambiguationData":[OSD([sQuery(id+"F16.wireOp",EDGE,"E27.bottom"),sQuery(id+"F16.wireOp",EDGE,"E27.top"),sQuery(id+"F16.wireOp",EDGE,"E27.left"),sQuery(id+"F16.wireOp",EDGE,"E27.right"),sQuery(id+"F16.wireOp",EDGE,"E28"),sQuery(id+"F16.wireOp",EDGE,"E29.0.1.0"),sQuery(id+"F16.wireOp",EDGE,"E29.0.2.0"),sQuery(id+"F16.wireOp",EDGE,"E29.0.3.0"),sQuery(id+"F16.wireOp",EDGE,"E29.0.4.0"),sQuery(id+"F16.wireOp",EDGE,"E29.0.5.0"),sQuery(id+"F16.wireOp",EDGE,"E29.0.6.0"),sQuery(id+"F16.wireOp",EDGE,"E29.0.7.0"),sQuery(id+"F16.wireOp",EDGE,"E29.0.8.0"),sQuery(id+"F16.wireOp",EDGE,"E29.0.9.0")])],"isStart":false});
            extrude(context, id + "F19", {"entities" : qUnion([Q0]), "endBound" : BoundingType.UP_TO_SURFACE, "depth" : 25.4 * mm, "endBoundEntityFace" : qUnion([Q1]), "offsetDistance" : 25.4 * mm});
        }
        {
            var Q0;
            Q0=qCreatedBy(makeId("Top.planeOp"),FACE);
            var sketch = newSketch(context, id + "F20", { "sketchPlane" : qUnion([Q0])});
            skLineSegment(sketch, "E34.bottom", {"start": v(-266.29, -43.6) * mm, "end": v(-256.26, -43.6) * mm});
            skLineSegment(sketch, "E34.top", {"start": v(-266.29, 40.42) * mm, "end": v(-256.26, 40.42) * mm});
            skLineSegment(sketch, "E34.left", {"start": v(-266.29, -43.6) * mm, "end": v(-266.29, 40.42) * mm});
            skLineSegment(sketch, "E34.right", {"start": v(-256.26, -43.6) * mm, "end": v(-256.26, 40.42) * mm});
            skCircle(sketch, "E35", {"center": v(-261.27, -39.78) * mm, "radius": 2.6 * mm});
            skPoint(sketch, "E35.centerSnap0", {"position": v(-261.27, -43.6) * mm});
            skCircle(sketch, "E36.0.1.0", {"center": v(-261.27, -32.29) * mm, "radius": 2.6 * mm});
            skCircle(sketch, "E36.0.2.0", {"center": v(-261.27, -24.8) * mm, "radius": 2.6 * mm});
            skCircle(sketch, "E36.0.3.0", {"center": v(-261.27, -17.3) * mm, "radius": 2.6 * mm});
            skCircle(sketch, "E36.0.4.0", {"center": v(-261.27, -9.81) * mm, "radius": 2.6 * mm});
            skCircle(sketch, "E36.0.5.0", {"center": v(-261.27, -2.32) * mm, "radius": 2.6 * mm});
            skCircle(sketch, "E36.0.6.0", {"center": v(-261.27, 5.18) * mm, "radius": 2.6 * mm});
            skCircle(sketch, "E36.0.7.0", {"center": v(-261.27, 12.67) * mm, "radius": 2.6 * mm});
            skCircle(sketch, "E36.0.8.0", {"center": v(-261.27, 20.16) * mm, "radius": 2.6 * mm});
            skCircle(sketch, "E36.0.9.0", {"center": v(-261.27, 27.65) * mm, "radius": 2.6 * mm});
            skCircle(sketch, "E36.0.10.0", {"center": v(-261.27, 35.15) * mm, "radius": 2.6 * mm});
            skLineSegment(sketch, "E36.direction1", {"start": v(-261.27, -39.78) * mm, "end": v(-242.65, -39.78) * mm, "construction": true});
            skLineSegment(sketch, "E36.direction2", {"start": v(-261.27, -39.78) * mm, "end": v(-261.27, -32.29) * mm, "construction": true});
            skSolve(sketch);
        }
        {
            var Q0;
            Q0=qCreatedBy(makeId("Top.planeOp"),FACE);
            var sketch = newSketch(context, id + "F21", { "sketchPlane" : qUnion([Q0])});
            skLineSegment(sketch, "E37.bottom", {"start": v(-208.94, -76.6) * mm, "end": v(-198.9, -76.6) * mm});
            skLineSegment(sketch, "E37.top", {"start": v(-208.94, -7.34) * mm, "end": v(-198.9, -7.34) * mm});
            skLineSegment(sketch, "E37.left", {"start": v(-208.94, -76.6) * mm, "end": v(-208.94, -7.34) * mm});
            skLineSegment(sketch, "E37.right", {"start": v(-198.9, -76.6) * mm, "end": v(-198.9, -7.34) * mm});
            skCircle(sketch, "E38", {"center": v(-203.92, -72.8) * mm, "radius": 2.6 * mm});
            skPoint(sketch, "E38.centerSnap0", {"position": v(-203.92, -76.6) * mm});
            skCircle(sketch, "E39.0.1.0", {"center": v(-203.92, -65.3) * mm, "radius": 2.6 * mm});
            skCircle(sketch, "E39.0.2.0", {"center": v(-203.92, -57.81) * mm, "radius": 2.6 * mm});
            skCircle(sketch, "E39.0.3.0", {"center": v(-203.92, -50.32) * mm, "radius": 2.6 * mm});
            skCircle(sketch, "E39.0.4.0", {"center": v(-203.92, -42.83) * mm, "radius": 2.6 * mm});
            skCircle(sketch, "E39.0.5.0", {"center": v(-203.92, -35.33) * mm, "radius": 2.6 * mm});
            skCircle(sketch, "E39.0.6.0", {"center": v(-203.92, -27.84) * mm, "radius": 2.6 * mm});
            skCircle(sketch, "E39.0.7.0", {"center": v(-203.92, -20.35) * mm, "radius": 2.6 * mm});
            skCircle(sketch, "E39.0.8.0", {"center": v(-203.92, -12.85) * mm, "radius": 2.6 * mm});
            skLineSegment(sketch, "E39.direction1", {"start": v(-203.92, -72.8) * mm, "end": v(-184.1, -72.8) * mm, "construction": true});
            skLineSegment(sketch, "E39.direction2", {"start": v(-203.92, -72.8) * mm, "end": v(-203.92, -65.3) * mm, "construction": true});
            skSolve(sketch);
        }
        {
            var Q0;
            Q0 = qSketchRegion(id + "F21", true);
            var Q1;
            Q1 = qSketchRegion(id + "F20", true);
            var Q2;
            Q2=makeQuery(id+"F17.opExtrude","CAP_FACE",FACE,{"disambiguationData":[OSD([sQuery(id+"F16.wireOp",EDGE,"E27.bottom"),sQuery(id+"F16.wireOp",EDGE,"E27.top"),sQuery(id+"F16.wireOp",EDGE,"E27.left"),sQuery(id+"F16.wireOp",EDGE,"E27.right"),sQuery(id+"F16.wireOp",EDGE,"E28"),sQuery(id+"F16.wireOp",EDGE,"E29.0.1.0"),sQuery(id+"F16.wireOp",EDGE,"E29.0.2.0"),sQuery(id+"F16.wireOp",EDGE,"E29.0.3.0"),sQuery(id+"F16.wireOp",EDGE,"E29.0.4.0"),sQuery(id+"F16.wireOp",EDGE,"E29.0.5.0"),sQuery(id+"F16.wireOp",EDGE,"E29.0.6.0"),sQuery(id+"F16.wireOp",EDGE,"E29.0.7.0"),sQuery(id+"F16.wireOp",EDGE,"E29.0.8.0"),sQuery(id+"F16.wireOp",EDGE,"E29.0.9.0")])],"isStart":false});
            extrude(context, id + "F22", {"entities" : qUnion([Q0, Q1]), "endBound" : BoundingType.UP_TO_SURFACE, "depth" : 25.4 * mm, "endBoundEntityFace" : qUnion([Q2]), "offsetDistance" : 25.4 * mm});
        }
        {
            var Q0;
            Q0=qCreatedBy(makeId("Top.planeOp"),FACE);
            var sketch = newSketch(context, id + "F23", { "sketchPlane" : qUnion([Q0])});
            skLineSegment(sketch, "E40.bottom", {"start": v(-239, 35.1) * mm, "end": v(-228.96, 35.1) * mm});
            skLineSegment(sketch, "E40.top", {"start": v(-239, 58.9) * mm, "end": v(-228.96, 58.9) * mm});
            skLineSegment(sketch, "E40.left", {"start": v(-239, 35.1) * mm, "end": v(-239, 58.9) * mm});
            skLineSegment(sketch, "E40.right", {"start": v(-228.96, 35.1) * mm, "end": v(-228.96, 58.9) * mm});
            skCircle(sketch, "E41", {"center": v(-233.97, 38.91) * mm, "radius": 2.6 * mm});
            skPoint(sketch, "E41.centerSnap0", {"position": v(-233.97, 35.1) * mm});
            skCircle(sketch, "E42.0.1.0", {"center": v(-233.97, 46.4) * mm, "radius": 2.6 * mm});
            skCircle(sketch, "E42.0.2.0", {"center": v(-233.97, 53.9) * mm, "radius": 2.6 * mm});
            skLineSegment(sketch, "E42.direction1", {"start": v(-233.97, 38.91) * mm, "end": v(-216.67, 38.91) * mm, "construction": true});
            skLineSegment(sketch, "E42.direction2", {"start": v(-233.97, 38.91) * mm, "end": v(-233.97, 46.4) * mm, "construction": true});
            skSolve(sketch);
        }
        {
            var Q0;
            Q0=makeQuery(id+"F23.imprint","IMPRINT",FACE,{"disambiguationData":[TD([[makeQuery(id+"F23.imprint","IMPRINT",EDGE,{"derivedFrom":sQuery(id+"F23.wireOp",EDGE,"E40.bottom")}),1.0]])]});
            var Q1;
            Q1=makeQuery(id+"F22.opExtrude","CAP_FACE",FACE,{"disambiguationData":[OSD([sQuery(id+"F20.wireOp",EDGE,"E34.bottom"),sQuery(id+"F20.wireOp",EDGE,"E34.top"),sQuery(id+"F20.wireOp",EDGE,"E34.left"),sQuery(id+"F20.wireOp",EDGE,"E34.right"),sQuery(id+"F20.wireOp",EDGE,"E35"),sQuery(id+"F20.wireOp",EDGE,"E36.0.1.0"),sQuery(id+"F20.wireOp",EDGE,"E36.0.2.0"),sQuery(id+"F20.wireOp",EDGE,"E36.0.3.0"),sQuery(id+"F20.wireOp",EDGE,"E36.0.4.0"),sQuery(id+"F20.wireOp",EDGE,"E36.0.5.0"),sQuery(id+"F20.wireOp",EDGE,"E36.0.6.0"),sQuery(id+"F20.wireOp",EDGE,"E36.0.7.0"),sQuery(id+"F20.wireOp",EDGE,"E36.0.8.0"),sQuery(id+"F20.wireOp",EDGE,"E36.0.9.0"),sQuery(id+"F20.wireOp",EDGE,"E36.0.10.0")])],"isStart":false});
            extrude(context, id + "F24", {"entities" : qUnion([Q0]), "endBound" : BoundingType.UP_TO_SURFACE, "depth" : 25.4 * mm, "endBoundEntityFace" : qUnion([Q1]), "offsetDistance" : 25.4 * mm});
        }
    });
